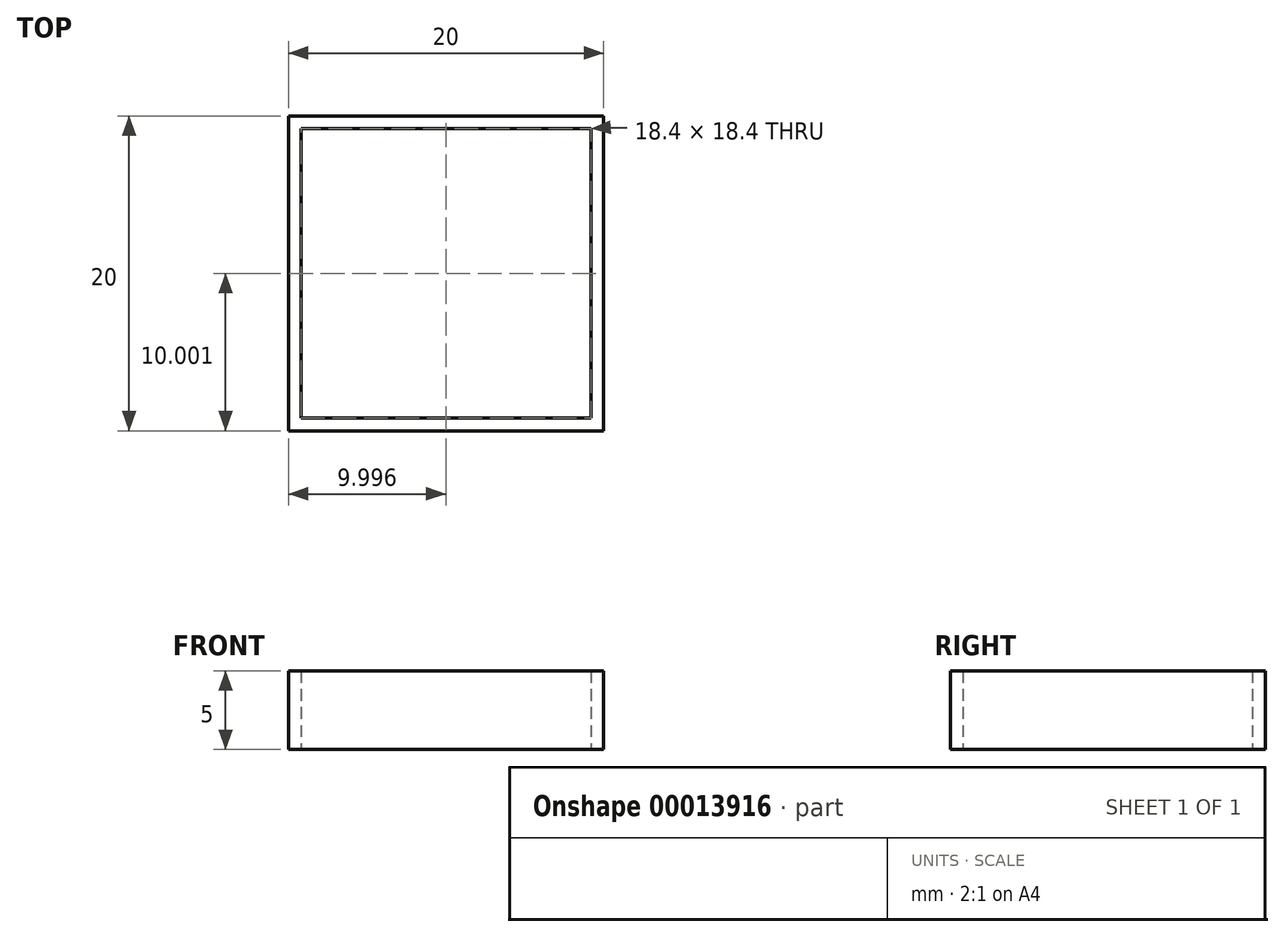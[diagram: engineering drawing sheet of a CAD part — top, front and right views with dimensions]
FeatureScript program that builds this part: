
annotation { "Feature Type Name" : "Feature", "Feature Type Description" : "" }
export const myFeature = defineFeature(function(context is Context, id is Id, definition is map)
    precondition{}
    {
        {
            var Q0;
            Q0=qCreatedBy(makeId("Top.planeOp"),FACE);
            var sketch = newSketch(context, id + "F0", { "sketchPlane" : qUnion([Q0])});
            skLineSegment(sketch, "E0.bottom", {"start": v(-8.75, 10.43) * mm, "end": v(11.25, 10.43) * mm});
            skLineSegment(sketch, "E0.top", {"start": v(-8.75, -9.57) * mm, "end": v(11.25, -9.57) * mm});
            skLineSegment(sketch, "E0.left", {"start": v(-8.75, 10.43) * mm, "end": v(-8.75, -9.57) * mm});
            skLineSegment(sketch, "E0.right", {"start": v(11.25, 10.43) * mm, "end": v(11.25, -9.57) * mm});
            skLineSegment(sketch, "E1.0", {"start": v(-7.95, -8.77) * mm, "end": v(10.45, -8.77) * mm});
            skLineSegment(sketch, "E1.1", {"start": v(-7.95, 9.63) * mm, "end": v(-7.95, -8.77) * mm});
            skLineSegment(sketch, "E1.2", {"start": v(-7.95, 9.63) * mm, "end": v(10.45, 9.63) * mm});
            skLineSegment(sketch, "E1.3", {"start": v(10.45, 9.63) * mm, "end": v(10.45, -8.77) * mm});
            skSolve(sketch);
        }
        {
            var Q0;
            Q0 = qSketchRegion(id + "F0", true);
            extrude(context, id + "F1", {"entities" : qUnion([Q0]), "depth" : 5 * mm});
        }
    });
